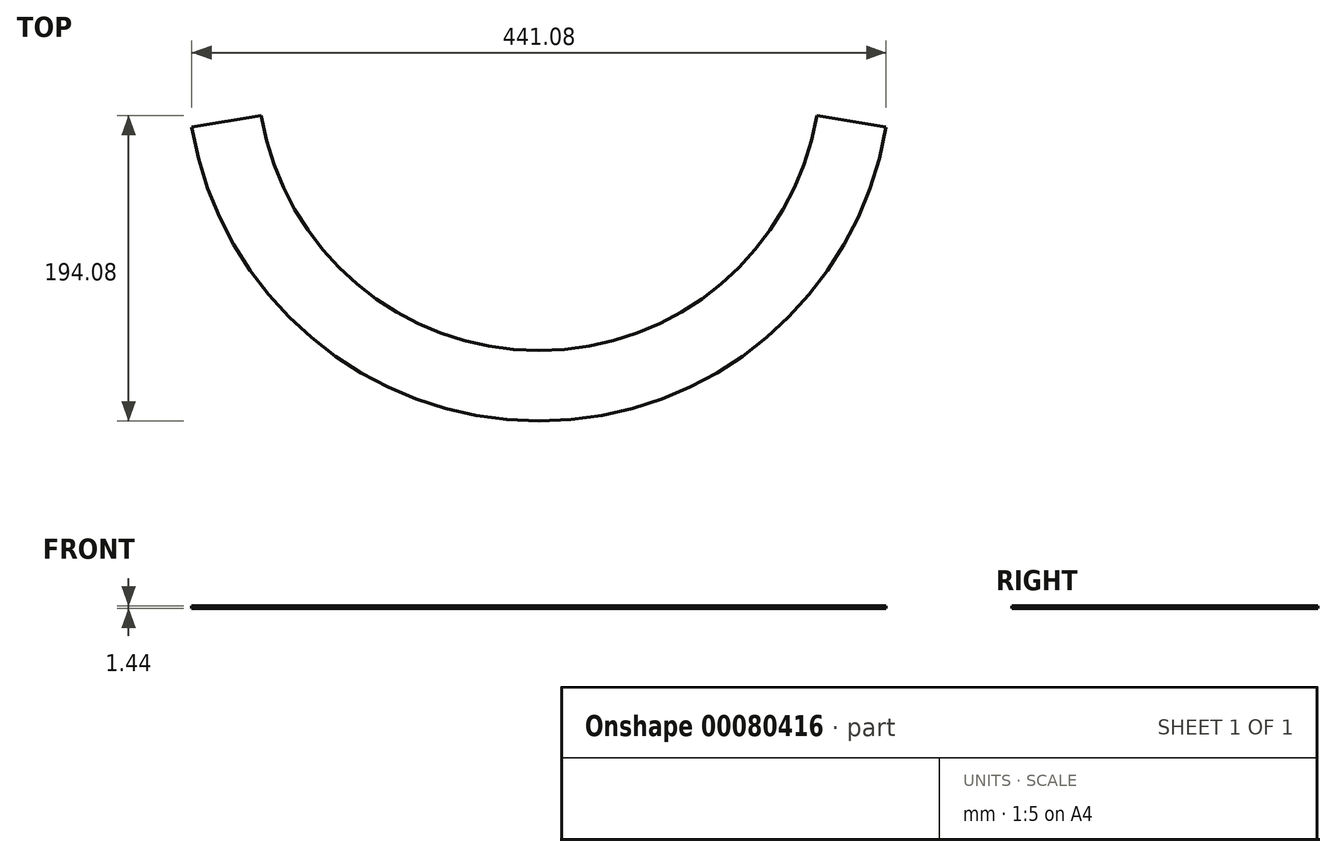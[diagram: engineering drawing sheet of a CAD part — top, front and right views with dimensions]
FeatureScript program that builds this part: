
annotation { "Feature Type Name" : "Feature", "Feature Type Description" : "" }
export const myFeature = defineFeature(function(context is Context, id is Id, definition is map)
    precondition{}
    {
        {
            var Q0;
            Q0=qCreatedBy(makeId("Top.planeOp"),FACE);
            var sketch = newSketch(context, id + "F0", { "sketchPlane" : qUnion([Q0])});
            skArc(sketch, "E0", {"start": v(-220.54, -36.9) * mm, "mid": v(0, -223.61) * mm, "end": v(220.54, -36.9) * mm});
            skArc(sketch, "E1", {"start": v(-176.44, -29.53) * mm, "mid": v(0, -178.9) * mm, "end": v(176.44, -29.53) * mm});
            skLineSegment(sketch, "E2", {"start": v(-220.54, -36.9) * mm, "end": v(-176.44, -29.53) * mm});
            skLineSegment(sketch, "E3", {"start": v(176.44, -29.53) * mm, "end": v(220.54, -36.9) * mm});
            skLineSegment(sketch, "E4", {"start": v(-176.44, -29.53) * mm, "end": v(0, 0) * mm, "construction": true});
            skLineSegment(sketch, "E5", {"start": v(176.44, -29.53) * mm, "end": v(0, 0) * mm, "construction": true});
            skSolve(sketch);
        }
        {
            var Q0;
            Q0=makeQuery(id+"F0.imprint","IMPRINT",FACE,{"disambiguationData":[TD([[makeQuery(id+"F0.imprint","IMPRINT",EDGE,{"derivedFrom":sQuery(id+"F0.wireOp",EDGE,"E0")}),1.0]])]});
            extrude(context, id + "F1", {"entities" : qUnion([Q0]), "endBound" : BoundingType.SYMMETRIC, "depth" : 1.45 * mm});
        }
    });
